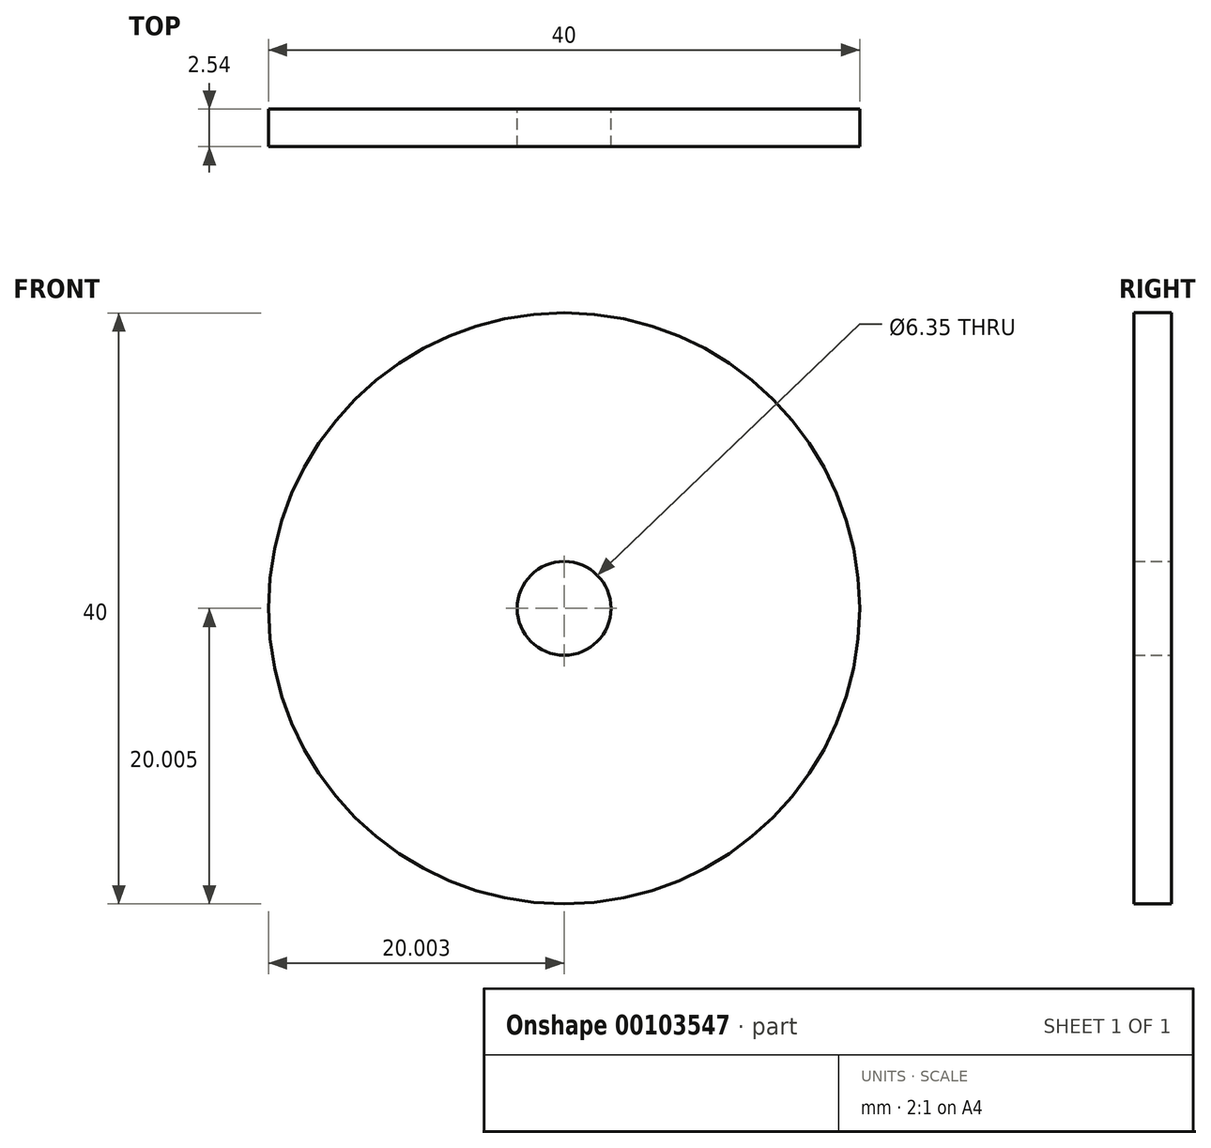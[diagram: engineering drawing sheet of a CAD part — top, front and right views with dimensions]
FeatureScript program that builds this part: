
annotation { "Feature Type Name" : "Feature", "Feature Type Description" : "" }
export const myFeature = defineFeature(function(context is Context, id is Id, definition is map)
    precondition{}
    {
        {
            var Q0;
            Q0=qCreatedBy(makeId("Front.planeOp"),FACE);
            var sketch = newSketch(context, id + "F0", { "sketchPlane" : qUnion([Q0])});
            skCircle(sketch, "E0", {"center": v(-7.29, 21.98) * mm, "radius": 20 * mm});
            skCircle(sketch, "E1", {"center": v(-7.29, 21.98) * mm, "radius": 3.18 * mm});
            skSolve(sketch);
        }
        {
            var Q0;
            Q0=makeQuery(id+"F0.imprint","IMPRINT",FACE,{"disambiguationData":[TD([[makeQuery(id+"F0.imprint","IMPRINT",EDGE,{"derivedFrom":sQuery(id+"F0.wireOp",EDGE,"E0")}),1.0]])]});
            extrude(context, id + "F1", {"entities" : qUnion([Q0]), "depth" : 2.54 * mm});
        }
    });
